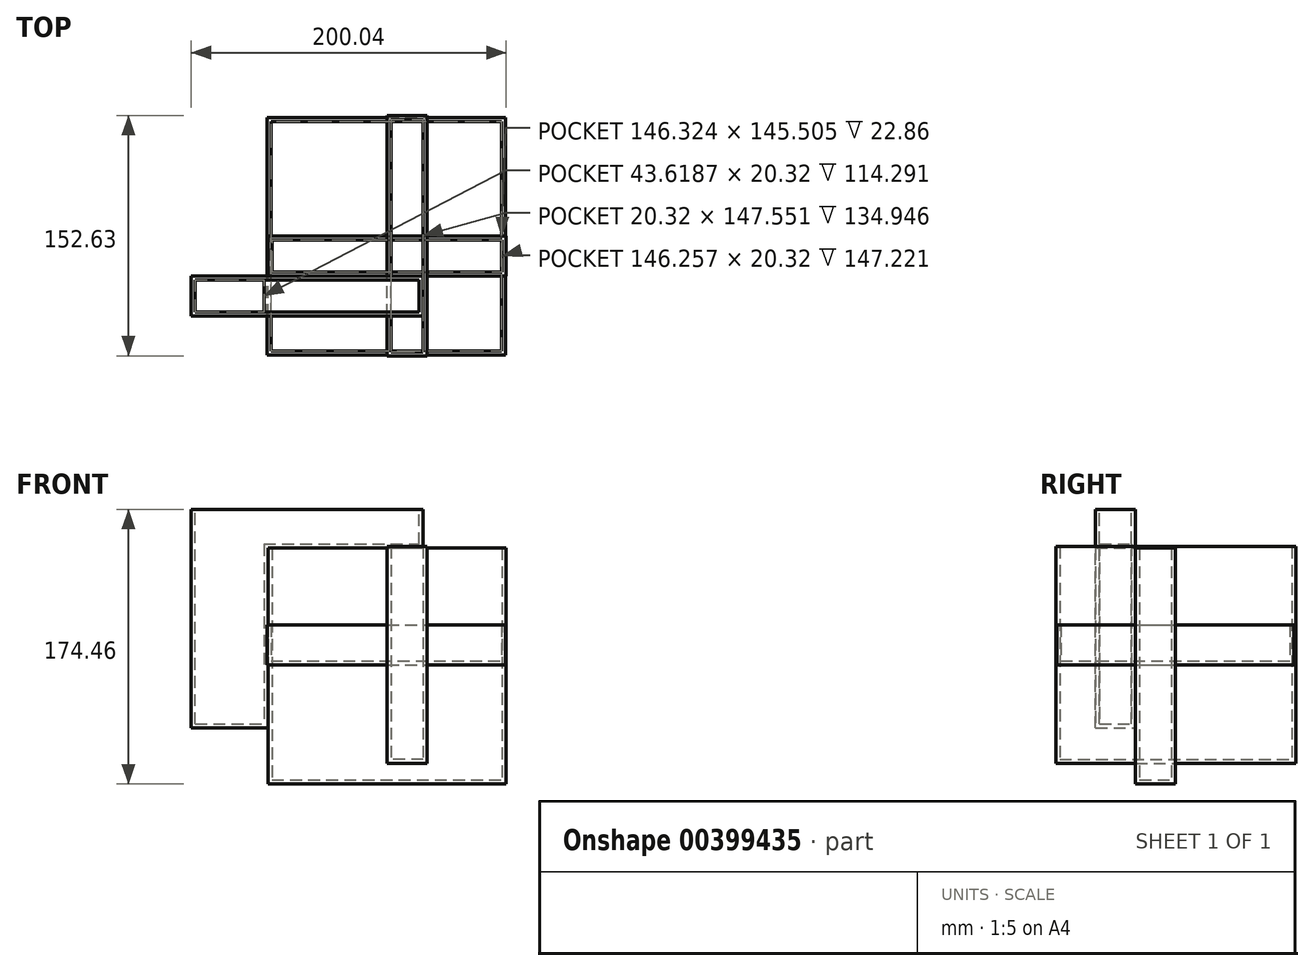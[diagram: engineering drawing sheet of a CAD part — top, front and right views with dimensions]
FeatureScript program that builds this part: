
annotation { "Feature Type Name" : "Feature", "Feature Type Description" : "" }
export const myFeature = defineFeature(function(context is Context, id is Id, definition is map)
    precondition{}
    {
        {
            var Q0;
            Q0=qCreatedBy(makeId("Front.planeOp"),FACE);
            var sketch = newSketch(context, id + "F0", { "sketchPlane" : qUnion([Q0])});
            skLineSegment(sketch, "E0.bottom", {"start": v(-75.67, 74.22) * mm, "end": v(75.67, 74.22) * mm});
            skLineSegment(sketch, "E0.top", {"start": v(-75.67, -75.54) * mm, "end": v(75.67, -75.54) * mm});
            skLineSegment(sketch, "E0.left", {"start": v(-75.67, 74.22) * mm, "end": v(-75.67, -75.54) * mm});
            skLineSegment(sketch, "E0.right", {"start": v(75.67, 74.22) * mm, "end": v(75.67, -75.54) * mm});
            skSolve(sketch);
        }
        {
            var Q0;
            Q0=makeQuery(id+"F0.imprint","IMPRINT",FACE,{"disambiguationData":[TD([[makeQuery(id+"F0.imprint","IMPRINT",EDGE,{"derivedFrom":sQuery(id+"F0.wireOp",EDGE,"E0.bottom")}),-1.0]])]});
            extrude(context, id + "F1", {"entities" : qUnion([Q0]), "depth" : 25.4 * mm});
        }
        {
            var Q0;
            Q0=makeQuery(id+"F1.opExtrude","CAP_FACE",FACE,{"disambiguationData":[OSD([sQuery(id+"F0.wireOp",EDGE,"E0.bottom"),sQuery(id+"F0.wireOp",EDGE,"E0.top"),sQuery(id+"F0.wireOp",EDGE,"E0.left"),sQuery(id+"F0.wireOp",EDGE,"E0.right")])],"isStart":false});
            var sketch = newSketch(context, id + "F2", { "sketchPlane" : qUnion([Q0])});
            skLineSegment(sketch, "E1.bottom", {"start": v(-124.37, -40.07) * mm, "end": v(22.94, -40.07) * mm});
            skLineSegment(sketch, "E1.top", {"start": v(-124.37, 98.92) * mm, "end": v(22.94, 98.92) * mm});
            skLineSegment(sketch, "E1.left", {"start": v(-124.37, -40.07) * mm, "end": v(-124.37, 98.92) * mm});
            skLineSegment(sketch, "E1.right", {"start": v(22.94, -40.07) * mm, "end": v(22.94, 98.92) * mm});
            skSolve(sketch);
        }
        {
            var Q0;
            {var subQ1=sQuery(id+"F2.wireOp",EDGE,"E1.top");Q0=makeQuery(id+"F2.imprint","IMPRINT",FACE,{"disambiguationData":[TD([[makeQuery(id+"F2.imprint","IMPRINT",EDGE,{"derivedFrom":subQ1}),-1.0]])]});}
            extrude(context, id + "F3", {"entities" : qUnion([Q0]), "depth" : 25.4 * mm});
        }
        {
            var Q0;
            Q0=qCreatedBy(makeId("Top.planeOp"),FACE);
            var sketch = newSketch(context, id + "F4", { "sketchPlane" : qUnion([Q0])});
            skLineSegment(sketch, "E2.bottom", {"start": v(-76.32, -75.5) * mm, "end": v(75.09, -75.5) * mm});
            skLineSegment(sketch, "E2.top", {"start": v(-76.32, 75.09) * mm, "end": v(75.09, 75.09) * mm});
            skLineSegment(sketch, "E2.left", {"start": v(-76.32, -75.5) * mm, "end": v(-76.32, 75.09) * mm});
            skLineSegment(sketch, "E2.right", {"start": v(75.09, -75.5) * mm, "end": v(75.09, 75.09) * mm});
            skSolve(sketch);
        }
        {
            var Q0;
            Q0=makeQuery(id+"F4.imprint","IMPRINT",FACE,{"disambiguationData":[TD([[makeQuery(id+"F4.imprint","IMPRINT",EDGE,{"derivedFrom":sQuery(id+"F4.wireOp",EDGE,"E2.bottom")}),1.0]])]});
            extrude(context, id + "F5", {"entities" : qUnion([Q0]), "depth" : 25.4 * mm});
        }
        {
            var Q0;
            Q0=qCreatedBy(makeId("Right.planeOp"),FACE);
            var sketch = newSketch(context, id + "F6", { "sketchPlane" : qUnion([Q0])});
            skLineSegment(sketch, "E3.bottom", {"start": v(-76.11, 75.17) * mm, "end": v(76.52, 75.17) * mm});
            skLineSegment(sketch, "E3.top", {"start": v(-76.11, -62.31) * mm, "end": v(76.52, -62.31) * mm});
            skLineSegment(sketch, "E3.left", {"start": v(-76.11, 75.17) * mm, "end": v(-76.11, -62.31) * mm});
            skLineSegment(sketch, "E3.right", {"start": v(76.52, 75.17) * mm, "end": v(76.52, -62.31) * mm});
            skSolve(sketch);
        }
        {
            var Q0;
            Q0=makeQuery(id+"F6.imprint","IMPRINT",FACE,{"disambiguationData":[TD([[makeQuery(id+"F6.imprint","IMPRINT",EDGE,{"derivedFrom":sQuery(id+"F6.wireOp",EDGE,"E3.bottom")}),-1.0]])]});
            extrude(context, id + "F7", {"entities" : qUnion([Q0]), "depth" : 25.4 * mm});
        }
        {
            var Q0;
            Q0=makeQuery(id+"F3.opExtrude","SWEPT_FACE",FACE,{"disambiguationData":[OSD([sQuery(id+"F2.wireOp",EDGE,"E1.top")])]});
            shell(context, id + "F8", {"entities" : qUnion([Q0]), "thickness" : 2.54 * mm});
        }
        {
            var Q0;
            Q0=makeQuery(id+"F7.opExtrude","SWEPT_FACE",FACE,{"disambiguationData":[OSD([sQuery(id+"F6.wireOp",EDGE,"E3.bottom")])]});
            shell(context, id + "F9", {"entities" : qUnion([Q0]), "thickness" : 2.54 * mm});
        }
        {
            var Q0;
            Q0=makeQuery(id+"F1.opExtrude","SWEPT_FACE",FACE,{"disambiguationData":[OSD([sQuery(id+"F0.wireOp",EDGE,"E0.bottom")])]});
            shell(context, id + "F10", {"entities" : qUnion([Q0]), "thickness" : 2.54 * mm});
        }
        {
            var Q0;
            Q0=makeQuery(id+"F5.opExtrude","CAP_FACE",FACE,{"disambiguationData":[OSD([sQuery(id+"F4.wireOp",EDGE,"E2.bottom"),sQuery(id+"F4.wireOp",EDGE,"E2.top"),sQuery(id+"F4.wireOp",EDGE,"E2.left"),sQuery(id+"F4.wireOp",EDGE,"E2.right")])],"isStart":false});
            shell(context, id + "F11", {"entities" : qUnion([Q0]), "thickness" : 2.54 * mm});
        }
    });
